# Revit family: CC_1W
name_source: partatom
category: Lighting Fixtures
revit_build: Autodesk Revit 2014 (Build: 20130308_1515(x64)
units: mm (PartAtom-declared; Revit-internal decimal feet)

## types (1)
- CC-1W
    Apparent Load = 24 VA
    Assembly Code = D5020200
    Connector Description = Lighting Connector
    Default Elevation = 48"
    Description = Sharp Cutoff and Visual Uniformity. The classic cylindrical design of the Curvilinear luminaire features a simple geometric shape for architectural relevance and is ideal for retail outlets or automotive dealerships. The luminaire family is designed for performance, providing energy efficiency, and glare control, all manufactured to Kim Lightings high standards for quality.
    Features = • TIR Optics
• Available in 595nm, 3000K, 4000K and 5000K standard CCT
• Type 1, 2, 3, 4, 4W, 5QM, 5QN, 5R, 5W distributions
• 0 - 10V dimming drivers standard
• IP66 optic assembly
    Fixture distribution = Direct
    Glass = Hubbell - Glass
    Gold = Hubbell - Gold
    Housing Material = Paint - Hubbell - Textured Camera Black
    Lamp = LED
    Load Classification = Lighting
    Manufacturer = KIM Lighting
    Model = Curvilinear Cutoff
    Power Factor = 1
    Product Documentation Link = https://hubbellcdn.com
    Product Link = https://www.hubbell.com
    URL = https://www.hubbell.com
    Voltage = 120 V
    Warranty = 5 years Warranty
    Wattage Comments = 24
    Watts = 24 W
    White = Paint - Hubbell - Matte White

## geometry (parser evidence)
native form markers: Sweep x6
no freeform markers — native parametric forms only
